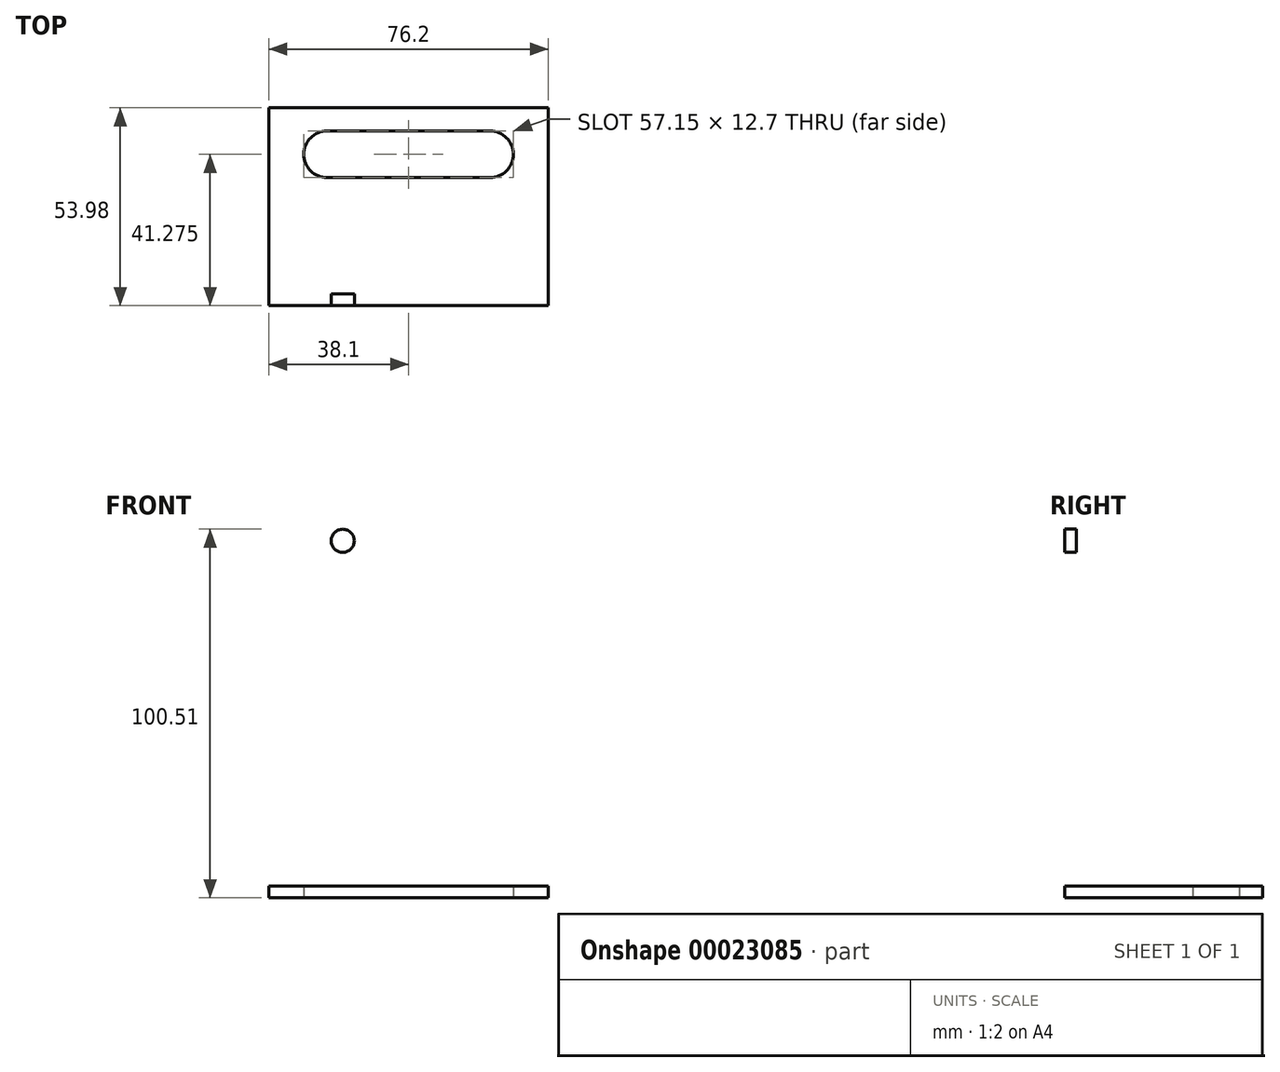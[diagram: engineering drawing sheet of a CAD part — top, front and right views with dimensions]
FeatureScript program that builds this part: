
annotation { "Feature Type Name" : "Feature", "Feature Type Description" : "" }
export const myFeature = defineFeature(function(context is Context, id is Id, definition is map)
    precondition{}
    {
        {
            var Q0;
            Q0=qCreatedBy(makeId("Top.planeOp"),FACE);
            var sketch = newSketch(context, id + "F0", { "sketchPlane" : qUnion([Q0])});
            skLineSegment(sketch, "E0", {"start": v(0, 0) * mm, "end": v(0, 53.98) * mm});
            skLineSegment(sketch, "E1", {"start": v(0, 53.98) * mm, "end": v(76.2, 53.98) * mm});
            skLineSegment(sketch, "E2", {"start": v(76.2, 53.98) * mm, "end": v(76.2, 0) * mm});
            skLineSegment(sketch, "E3", {"start": v(76.2, 0) * mm, "end": v(0, 0) * mm});
            skLineSegment(sketch, "E4", {"start": v(0, 41.27) * mm, "end": v(76.2, 41.27) * mm, "construction": true});
            skLineSegment(sketch, "E5", {"start": v(15.88, 53.98) * mm, "end": v(15.88, 0) * mm, "construction": true});
            skLineSegment(sketch, "E6", {"start": v(60.33, 53.98) * mm, "end": v(60.33, 0) * mm, "construction": true});
            skArc(sketch, "E7", {"start": v(15.88, 47.62) * mm, "mid": v(9.53, 41.27) * mm, "end": v(15.88, 34.92) * mm});
            skArc(sketch, "E8", {"start": v(60.33, 34.92) * mm, "mid": v(66.68, 41.27) * mm, "end": v(60.33, 47.62) * mm});
            skLineSegment(sketch, "E9.bottom", {"start": v(15.88, 47.62) * mm, "end": v(60.33, 47.62) * mm});
            skLineSegment(sketch, "E9.top", {"start": v(15.88, 34.92) * mm, "end": v(60.33, 34.92) * mm});
            skSolve(sketch);
        }
        {
            var Q0;
            Q0=makeQuery(id+"F0.imprint","IMPRINT",FACE,{"disambiguationData":[TD([[makeQuery(id+"F0.imprint","IMPRINT",EDGE,{"derivedFrom":sQuery(id+"F0.wireOp",EDGE,"E0")}),-1.0]])]});
            extrude(context, id + "F1", {"entities" : qUnion([Q0]), "depth" : 3.17 * mm});
        }
        {
            var Q0;
            Q0=makeQuery(id+"F1.opExtrude","CAP_FACE",FACE,{"disambiguationData":[OSD([sQuery(id+"F0.wireOp",EDGE,"E0"),sQuery(id+"F0.wireOp",EDGE,"E1"),sQuery(id+"F0.wireOp",EDGE,"E2"),sQuery(id+"F0.wireOp",EDGE,"E3"),sQuery(id+"F0.wireOp",EDGE,"E7"),sQuery(id+"F0.wireOp",EDGE,"E8"),sQuery(id+"F0.wireOp",EDGE,"E9.bottom"),sQuery(id+"F0.wireOp",EDGE,"E9.top")])],"isStart":false});
            var sketch = newSketch(context, id + "F2", { "sketchPlane" : qUnion([Q0])});
            skLineSegment(sketch, "E10", {"start": v(0, 3.17) * mm, "end": v(76.2, 3.18) * mm});
            skSolve(sketch);
        }
        {
            var Q0;
            {var subQ1=sQuery(id+"F2.wireOp",EDGE,"E10");Q0=makeQuery(id+"F2.imprint","IMPRINT",FACE,{"disambiguationData":[TD([[makeQuery(id+"F2.imprint","IMPRINT",EDGE,{"derivedFrom":subQ1}),-1.0]])]});}
            extrude(context, id + "F3", {"entities" : qUnion([Q0]), "operationType" : NewBodyOperationType.ADD, "depth" : 76.2 * mm});
        }
        {
            var Q0;
            Q0=makeQuery(id+"F3.opExtrude","SWEPT_FACE",FACE,{"disambiguationData":[OSD([sQuery(id+"F2.wireOp",EDGE,"E10")])]});
            var sketch = newSketch(context, id + "F4", { "sketchPlane" : qUnion([Q0])});
            skCircle(sketch, "E11", {"center": v(-38.1, 79.38) * mm, "radius": 38.1 * mm});
            skSolve(sketch);
        }
        {
            var Q0;
            {var subQ0=sQuery(id+"F2.wireOp",EDGE,"E10");var subQ1=makeQuery(id+"F3.opExtrude","CAP_EDGE",EDGE,{"disambiguationData":[OSD([subQ0])],"isStart":false});Q0=makeQuery(id+"F4.imprint","IMPRINT",FACE,{"disambiguationData":[TD([[makeQuery(id+"F4.imprint","IMPRINT",EDGE,{"derivedFrom":subQ1}),-1.0]])]});}
            extrude(context, id + "F5", {"entities" : qUnion([Q0]), "operationType" : NewBodyOperationType.ADD, "oppositeDirection" : true, "depth" : 3.17 * mm});
        }
        {
            var Q0;
            {var subQ0=sQuery(id+"F0.wireOp",EDGE,"E3");Q0=makeQuery(id+"F5.boolean.opBoolean","MERGE",FACE,{"derivedFrom":[makeQuery(id+"F3.boolean.opBoolean","MERGE",FACE,{"derivedFrom":[makeQuery(id+"F1.opExtrude","SWEPT_FACE",FACE,{"disambiguationData":[OSD([subQ0])]}),makeQuery(id+"F3.opExtrude","SWEPT_FACE",FACE,{"disambiguationData":[OSD([subQ0])]})]}),makeQuery(id+"F5.opExtrude","CAP_FACE",FACE,{"disambiguationData":[OSD([sQuery(id+"F2.wireOp",EDGE,"E10"),sQuery(id+"F4.wireOp",EDGE,"E11")])],"isStart":false})]});}
            var sketch = newSketch(context, id + "F6", { "sketchPlane" : qUnion([Q0])});
            skCircle(sketch, "E12", {"center": v(38.1, 79.38) * mm, "radius": 12.7 * mm});
            skSolve(sketch);
        }
        {
            var Q0;
            Q0=makeQuery(id+"F6.imprint","IMPRINT",FACE,{"disambiguationData":[TD([[makeQuery(id+"F6.imprint","IMPRINT",EDGE,{"derivedFrom":sQuery(id+"F6.wireOp",EDGE,"E12")}),1.0]])]});
            extrude(context, id + "F7", {"entities" : qUnion([Q0]), "operationType" : NewBodyOperationType.REMOVE, "oppositeDirection" : true, "depth" : 25.4 * mm});
        }
        {
            var Q0;
            {var subQ0=sQuery(id+"F2.wireOp",EDGE,"E10");Q0=makeQuery(id+"F5.boolean.opBoolean","MERGE",FACE,{"derivedFrom":[makeQuery(id+"F3.opExtrude","SWEPT_FACE",FACE,{"disambiguationData":[OSD([subQ0])]}),makeQuery(id+"F5.opExtrude","CAP_FACE",FACE,{"disambiguationData":[OSD([subQ0,sQuery(id+"F4.wireOp",EDGE,"E11")])],"isStart":true})]});}
            var sketch = newSketch(context, id + "F8", { "sketchPlane" : qUnion([Q0])});
            skLineSegment(sketch, "E13", {"start": v(-38.1, 79.38) * mm, "end": v(-38.1, 117.47) * mm, "construction": true});
            skLineSegment(sketch, "E14", {"start": v(-38.1, 79.38) * mm, "end": v(-76.2, 79.38) * mm, "construction": true});
            skLineSegment(sketch, "E15", {"start": v(-38.1, 79.38) * mm, "end": v(0, 79.38) * mm, "construction": true});
            skLineSegment(sketch, "E16", {"start": v(-38.1, 79.38) * mm, "end": v(-65.04, 106.32) * mm, "construction": true});
            skLineSegment(sketch, "E17", {"start": v(-38.1, 79.38) * mm, "end": v(-11.16, 106.32) * mm, "construction": true});
            skCircle(sketch, "E18", {"center": v(-56.06, 97.34) * mm, "radius": 3.18 * mm});
            skCircle(sketch, "E19", {"center": v(-38.1, 79.38) * mm, "radius": 25.4 * mm});
            skCircle(sketch, "E20.1.0", {"center": v(-56.06, 61.41) * mm, "radius": 3.18 * mm});
            skCircle(sketch, "E20.2.0", {"center": v(-20.14, 61.41) * mm, "radius": 3.18 * mm});
            skCircle(sketch, "E20.3.0", {"center": v(-20.14, 97.34) * mm, "radius": 3.18 * mm});
            skSolve(sketch);
        }
        {
            var Q0;
            {var subQ0=sQuery(id+"F8.wireOp",EDGE,"E20.3.0");var subQ1=sQuery(id+"F8.wireOp",EDGE,"E19");var subQ3=makeQuery(id+"F8.imprint","INTERSECT",VERTEX,{"disambiguationData":[OD(0.0)],"derivedFrom":[subQ1,subQ0]});Q0=makeQuery(id+"F8.imprint","IMPRINT",FACE,{"disambiguationData":[TD([[makeQuery(id+"F8.imprint","IMPRINT",EDGE,{"disambiguationData":[TD([[subQ3,1.0]])],"derivedFrom":subQ1}),-1.0]])]});}
            var Q1;
            {var subQ0=sQuery(id+"F8.wireOp",EDGE,"E20.3.0");var subQ1=sQuery(id+"F8.wireOp",EDGE,"E19");var subQ3=makeQuery(id+"F8.imprint","INTERSECT",VERTEX,{"disambiguationData":[OD(0.0)],"derivedFrom":[subQ1,subQ0]});Q1=makeQuery(id+"F8.imprint","IMPRINT",FACE,{"disambiguationData":[TD([[makeQuery(id+"F8.imprint","IMPRINT",EDGE,{"disambiguationData":[TD([[subQ3,1.0]])],"derivedFrom":subQ1}),1.0]])]});}
            var Q2;
            {var subQ0=sQuery(id+"F8.wireOp",EDGE,"E19");var subQ1=sQuery(id+"F8.wireOp",EDGE,"E18");var subQ3=makeQuery(id+"F8.imprint","INTERSECT",VERTEX,{"disambiguationData":[OD(0.0)],"derivedFrom":[subQ1,subQ0]});Q2=makeQuery(id+"F8.imprint","IMPRINT",FACE,{"disambiguationData":[TD([[makeQuery(id+"F8.imprint","IMPRINT",EDGE,{"disambiguationData":[TD([[subQ3,-1.0]])],"derivedFrom":subQ1}),1.0]])]});}
            var Q3;
            {var subQ0=sQuery(id+"F8.wireOp",EDGE,"E19");var subQ1=sQuery(id+"F8.wireOp",EDGE,"E18");var subQ3=makeQuery(id+"F8.imprint","INTERSECT",VERTEX,{"disambiguationData":[OD(0.0)],"derivedFrom":[subQ1,subQ0]});Q3=makeQuery(id+"F8.imprint","IMPRINT",FACE,{"disambiguationData":[TD([[makeQuery(id+"F8.imprint","IMPRINT",EDGE,{"disambiguationData":[TD([[subQ3,1.0]])],"derivedFrom":subQ1}),1.0]])]});}
            var Q4;
            {var subQ0=sQuery(id+"F8.wireOp",EDGE,"E20.1.0");var subQ1=sQuery(id+"F8.wireOp",EDGE,"E19");var subQ3=makeQuery(id+"F8.imprint","INTERSECT",VERTEX,{"disambiguationData":[OD(0.0)],"derivedFrom":[subQ1,subQ0]});Q4=makeQuery(id+"F8.imprint","IMPRINT",FACE,{"disambiguationData":[TD([[makeQuery(id+"F8.imprint","IMPRINT",EDGE,{"disambiguationData":[TD([[subQ3,-1.0]])],"derivedFrom":subQ1}),1.0]])]});}
            var Q5;
            {var subQ0=sQuery(id+"F8.wireOp",EDGE,"E20.1.0");var subQ1=sQuery(id+"F8.wireOp",EDGE,"E19");var subQ3=makeQuery(id+"F8.imprint","INTERSECT",VERTEX,{"disambiguationData":[OD(0.0)],"derivedFrom":[subQ1,subQ0]});Q5=makeQuery(id+"F8.imprint","IMPRINT",FACE,{"disambiguationData":[TD([[makeQuery(id+"F8.imprint","IMPRINT",EDGE,{"disambiguationData":[TD([[subQ3,-1.0]])],"derivedFrom":subQ1}),-1.0]])]});}
            var Q6;
            {var subQ0=sQuery(id+"F8.wireOp",EDGE,"E20.2.0");var subQ1=sQuery(id+"F8.wireOp",EDGE,"E19");var subQ3=makeQuery(id+"F8.imprint","INTERSECT",VERTEX,{"disambiguationData":[OD(0.0)],"derivedFrom":[subQ1,subQ0]});Q6=makeQuery(id+"F8.imprint","IMPRINT",FACE,{"disambiguationData":[TD([[makeQuery(id+"F8.imprint","IMPRINT",EDGE,{"disambiguationData":[TD([[subQ3,-1.0]])],"derivedFrom":subQ1}),-1.0]])]});}
            var Q7;
            {var subQ0=sQuery(id+"F8.wireOp",EDGE,"E20.2.0");var subQ1=sQuery(id+"F8.wireOp",EDGE,"E19");var subQ3=makeQuery(id+"F8.imprint","INTERSECT",VERTEX,{"disambiguationData":[OD(0.0)],"derivedFrom":[subQ1,subQ0]});Q7=makeQuery(id+"F8.imprint","IMPRINT",FACE,{"disambiguationData":[TD([[makeQuery(id+"F8.imprint","IMPRINT",EDGE,{"disambiguationData":[TD([[subQ3,-1.0]])],"derivedFrom":subQ1}),1.0]])]});}
            extrude(context, id + "F9", {"entities" : qUnion([Q0, Q1, Q2, Q3, Q4, Q5, Q6, Q7]), "operationType" : NewBodyOperationType.REMOVE, "oppositeDirection" : true, "depth" : 25.4 * mm});
        }
    });
